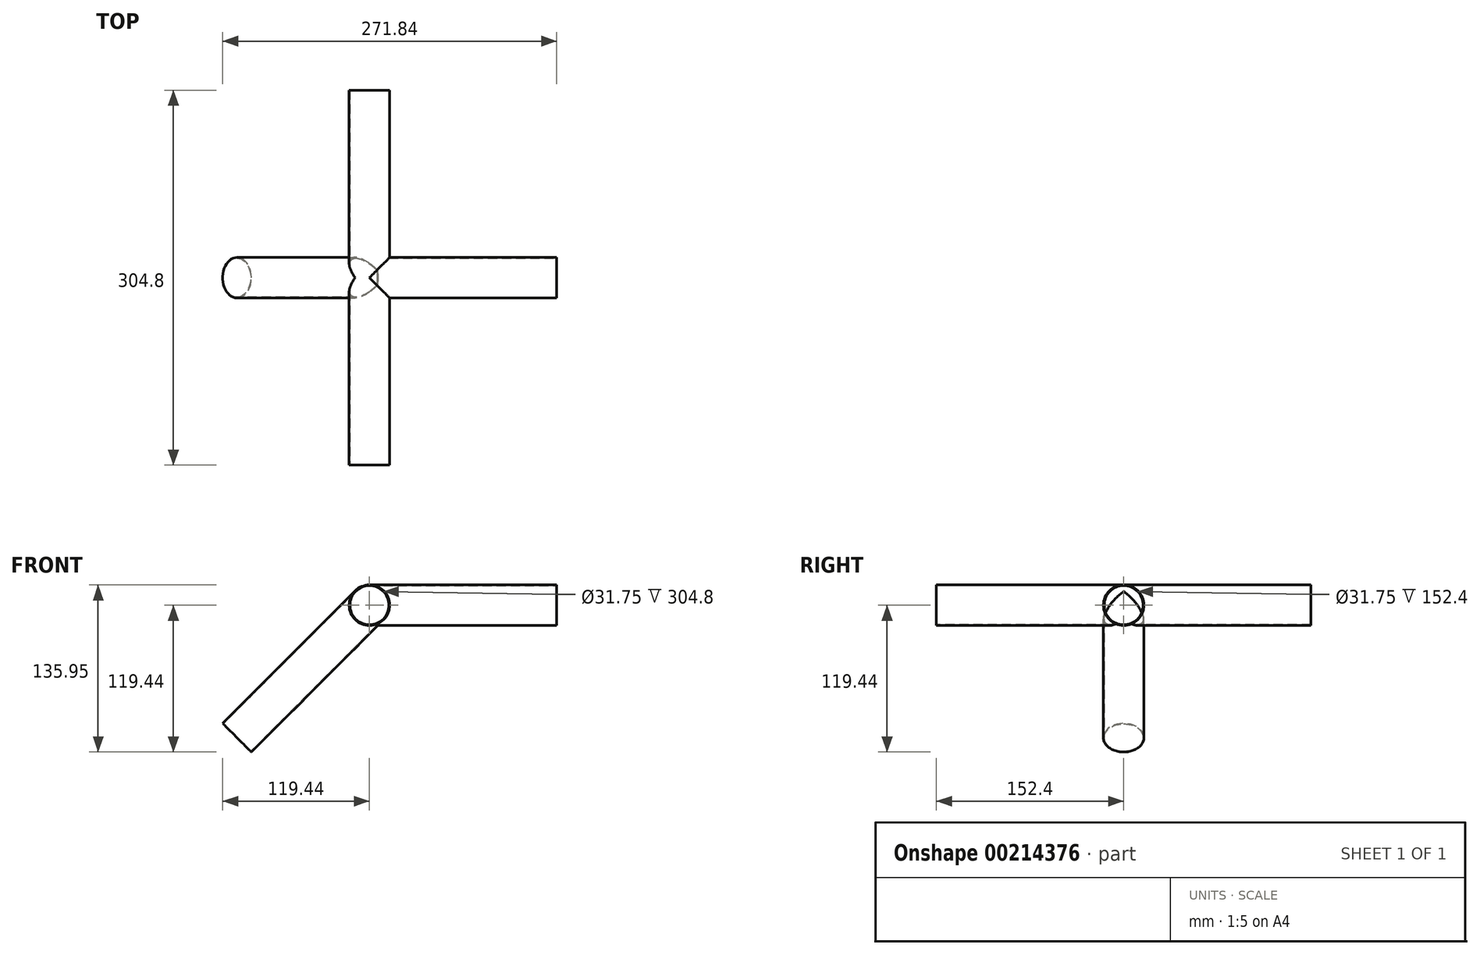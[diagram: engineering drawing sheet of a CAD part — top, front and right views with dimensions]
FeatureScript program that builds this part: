
annotation { "Feature Type Name" : "Feature", "Feature Type Description" : "" }
export const myFeature = defineFeature(function(context is Context, id is Id, definition is map)
    precondition{}
    {
        {
            var Q0;
            Q0=qCreatedBy(makeId("Front.planeOp"),FACE);
            var sketch = newSketch(context, id + "F0", { "sketchPlane" : qUnion([Q0])});
            skCircle(sketch, "E0", {"center": v(0, 0) * mm, "radius": 16.51 * mm});
            skSolve(sketch);
        }
        {
            var Q0;
            Q0 = qSketchRegion(id + "F0", true);
            extrude(context, id + "F1", {"entities" : qUnion([Q0]), "depth" : 152.4 * mm, "hasSecondDirection" : true, "secondDirectionOppositeDirection" : true, "secondDirectionDepth" : 152.4 * mm});
        }
        {
            var Q0;
            Q0=qCreatedBy(makeId("Right.planeOp"),FACE);
            var sketch = newSketch(context, id + "F2", { "sketchPlane" : qUnion([Q0])});
            skCircle(sketch, "E1", {"center": v(0, 0) * mm, "radius": 16.51 * mm});
            skSolve(sketch);
        }
        {
            var Q0;
            Q0 = qSketchRegion(id + "F2", true);
            extrude(context, id + "F3", {"entities" : qUnion([Q0]), "operationType" : NewBodyOperationType.ADD, "depth" : 152.4 * mm});
        }
        {
            var Q0;
            Q0=qCreatedBy(makeId("Right.planeOp"),FACE);
            var Q1;
            Q1=qCreatedBy(makeId("Top.planeOp"),FACE);
            cPlane(context, id + "F4", {"entities" : qUnion([Q0, Q1]), "cplaneType" : CPlaneType.MID_PLANE, "offset" : 25.4 * mm, "flipAlignment" : true, "width" : 152.4 * mm, "height" : 152.4 * mm});
        }
        {
            var Q0;
            Q0=qCreatedBy(id+"F4.planeOp",FACE);
            var sketch = newSketch(context, id + "F5", { "sketchPlane" : qUnion([Q0])});
            skCircle(sketch, "E2", {"center": v(0, 0) * mm, "radius": 16.51 * mm});
            skSolve(sketch);
        }
        {
            var Q0;
            Q0 = qSketchRegion(id + "F5", true);
            extrude(context, id + "F6", {"entities" : qUnion([Q0]), "operationType" : NewBodyOperationType.ADD, "oppositeDirection" : true, "depth" : 152.4 * mm});
        }
        {
            var Q0;
            Q0=makeQuery(id+"F1.opExtrude","CAP_FACE",FACE,{"disambiguationData":[OSD([sQuery(id+"F0.wireOp",EDGE,"E0")])],"isStart":false});
            var sketch = newSketch(context, id + "F7", { "sketchPlane" : qUnion([Q0])});
            skCircle(sketch, "E3", {"center": v(0, 0) * mm, "radius": 15.88 * mm});
            skSolve(sketch);
        }
        {
            var Q0;
            Q0 = qSketchRegion(id + "F7", true);
            extrude(context, id + "F8", {"entities" : qUnion([Q0]), "operationType" : NewBodyOperationType.REMOVE, "endBound" : BoundingType.THROUGH_ALL, "oppositeDirection" : true, "depth" : 25.4 * mm});
        }
        {
            var Q0;
            Q0=makeQuery(id+"F3.opExtrude","CAP_FACE",FACE,{"disambiguationData":[OSD([sQuery(id+"F2.wireOp",EDGE,"E1")])],"isStart":false});
            var sketch = newSketch(context, id + "F9", { "sketchPlane" : qUnion([Q0])});
            skCircle(sketch, "E4", {"center": v(0, 0) * mm, "radius": 15.88 * mm});
            skSolve(sketch);
        }
        {
            var Q0;
            Q0 = qSketchRegion(id + "F9", true);
            var Q1;
            Q1=makeQuery(id+"F8.boolean.opBoolean","COPY",FACE,{"derivedFrom":makeQuery(id+"F8.opExtrude","SWEPT_FACE",FACE,{"disambiguationData":[OSD([sQuery(id+"F7.wireOp",EDGE,"E3")])]})});
            extrude(context, id + "F10", {"entities" : qUnion([Q0]), "operationType" : NewBodyOperationType.REMOVE, "endBound" : BoundingType.UP_TO_SURFACE, "oppositeDirection" : true, "endBoundEntityFace" : qUnion([Q1]), "depth" : 25.4 * mm});
        }
        {
            var Q0;
            Q0=makeQuery(id+"F6.opExtrude","CAP_FACE",FACE,{"disambiguationData":[OSD([sQuery(id+"F5.wireOp",EDGE,"E2")])],"isStart":false});
            var sketch = newSketch(context, id + "F11", { "sketchPlane" : qUnion([Q0])});
            skCircle(sketch, "E5", {"center": v(0, 0) * mm, "radius": 15.88 * mm});
            skSolve(sketch);
        }
        {
            var Q0;
            Q0 = qSketchRegion(id + "F11", true);
            var Q1;
            Q1=makeQuery(id+"F8.boolean.opBoolean","COPY",FACE,{"derivedFrom":makeQuery(id+"F8.opExtrude","SWEPT_FACE",FACE,{"disambiguationData":[OSD([sQuery(id+"F7.wireOp",EDGE,"E3")])]})});
            extrude(context, id + "F12", {"entities" : qUnion([Q0]), "operationType" : NewBodyOperationType.REMOVE, "endBound" : BoundingType.UP_TO_SURFACE, "oppositeDirection" : true, "endBoundEntityFace" : qUnion([Q1]), "depth" : 25.4 * mm});
        }
    });
